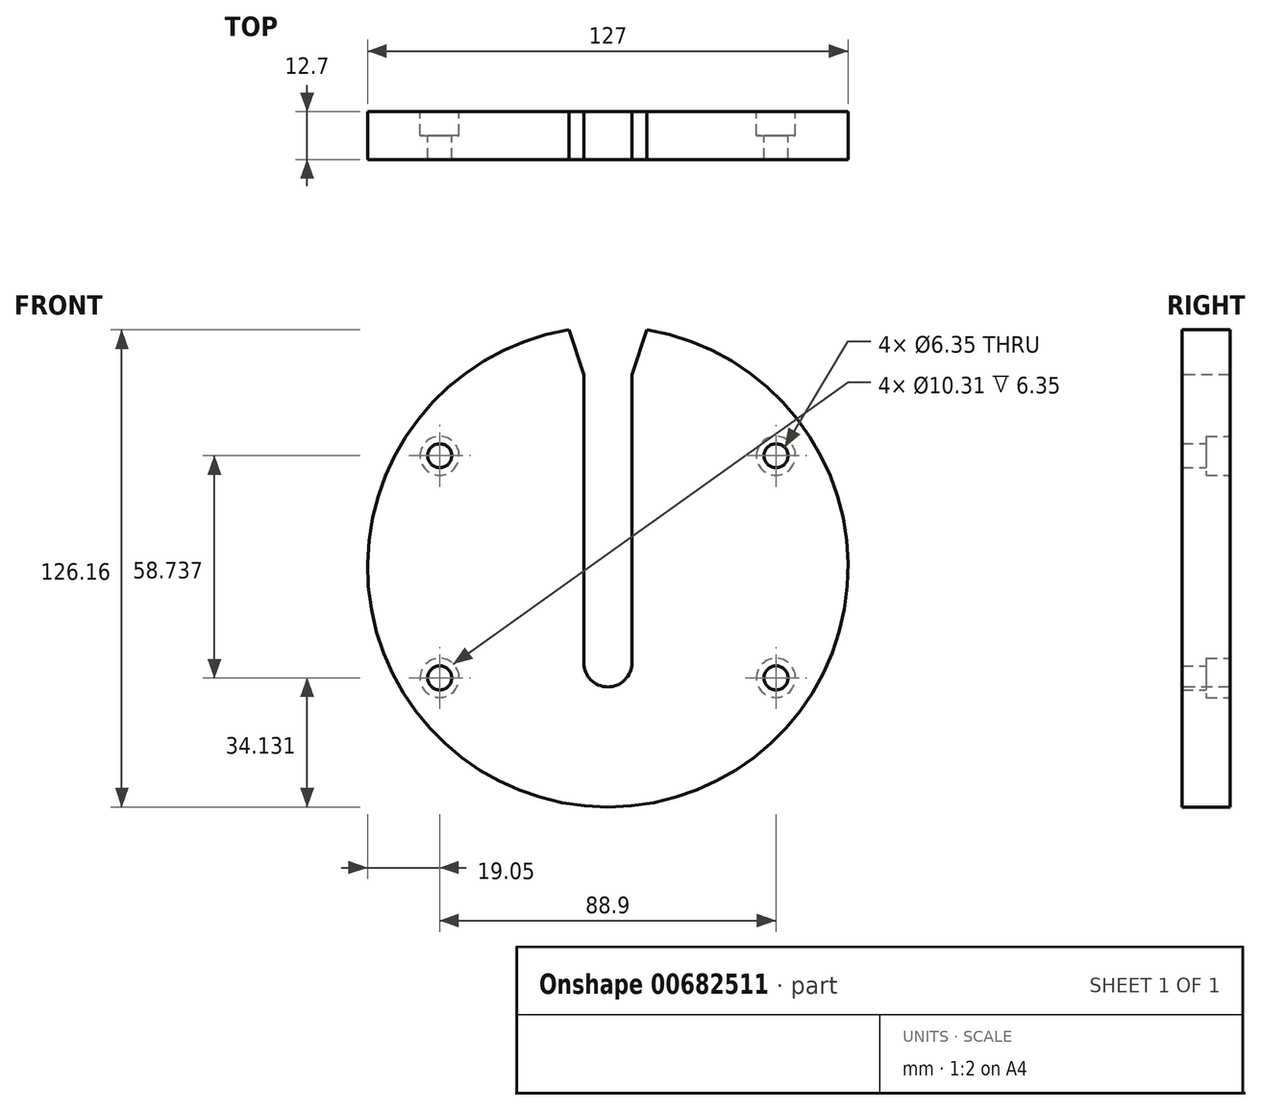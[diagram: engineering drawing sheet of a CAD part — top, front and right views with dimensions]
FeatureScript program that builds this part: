
annotation { "Feature Type Name" : "Feature", "Feature Type Description" : "" }
export const myFeature = defineFeature(function(context is Context, id is Id, definition is map)
    precondition{}
    {
        {
            var Q0;
            Q0=qCreatedBy(makeId("Front.planeOp"),FACE);
            var sketch = newSketch(context, id + "F0", { "sketchPlane" : qUnion([Q0])});
            skPoint(sketch, "E0", {"position": v(-44.45, 29.37) * mm});
            skPoint(sketch, "E1", {"position": v(44.45, 29.37) * mm});
            skPoint(sketch, "E2", {"position": v(44.45, -29.37) * mm});
            skPoint(sketch, "E3", {"position": v(-44.45, -29.37) * mm});
            skLineSegment(sketch, "E4", {"start": v(0, 0) * mm, "end": v(0, 0) * mm});
            skCircle(sketch, "E5", {"center": v(0, 0) * mm, "radius": 63.5 * mm});
            skSolve(sketch);
        }
        {
            var Q0;
            Q0=makeQuery(id+"F0.imprint","IMPRINT",FACE,{"disambiguationData":[TD([[makeQuery(id+"F0.imprint","IMPRINT",EDGE,{"derivedFrom":sQuery(id+"F0.wireOp",EDGE,"0SG29FPq-SwXB-MbIm-qeFK-cjPBrF2aFsSZ.bottom")}),1.0]])]});
            var Q1;
            Q1=makeQuery(id+"F0.imprint","IMPRINT",FACE,{"disambiguationData":[TD([[makeQuery(id+"F0.imprint","IMPRINT",EDGE,{"derivedFrom":sQuery(id+"F0.wireOp",EDGE,"0SG29FPq-SwXB-MbIm-qeFK-cjPBrF2aFsSZ.top")}),-1.0]])]});
            var Q2;
            Q2=makeQuery(id+"F0.imprint","IMPRINT",FACE,{"disambiguationData":[TD([[makeQuery(id+"F0.imprint","IMPRINT",EDGE,{"derivedFrom":sQuery(id+"F0.wireOp",EDGE,"E5")}),1.0]])]});
            extrude(context, id + "F1", {"entities" : qUnion([Q0, Q1, Q2]), "depth" : 12.7 * mm, "offsetDistance" : 25.4 * mm});
        }
        {
            var Q0;
            Q0=makeQuery(id+"F1.opExtrude","CAP_FACE",FACE,{"disambiguationData":[OSD([sQuery(id+"F0.wireOp",EDGE,"E5")])],"isStart":false});
            var sketch = newSketch(context, id + "F2", { "sketchPlane" : qUnion([Q0])});
            skLineSegment(sketch, "E6", {"start": v(-6.35, 50.8) * mm, "end": v(-6.35, -25.4) * mm});
            skLineSegment(sketch, "E7", {"start": v(6.35, -25.4) * mm, "end": v(6.35, 50.8) * mm});
            skArc(sketch, "E8", {"start": v(-6.35, -25.4) * mm, "mid": v(0, -31.75) * mm, "end": v(6.35, -25.4) * mm});
            skLineSegment(sketch, "E9", {"start": v(10.31, 62.66) * mm, "end": v(6.35, 50.8) * mm});
            skLineSegment(sketch, "E10", {"start": v(-6.35, 50.8) * mm, "end": v(-10.31, 62.66) * mm});
            skPoint(sketch, "E11.orphan", {"position": v(6.35, 63.18) * mm});
            skSolve(sketch);
        }
        {
            var Q0;
            {var subQ0=sQuery(id+"F2.wireOp",EDGE,"E6");Q0=makeQuery(id+"F2.imprint","IMPRINT",FACE,{"disambiguationData":[TD([[makeQuery(id+"F2.imprint","IMPRINT",EDGE,{"derivedFrom":subQ0}),1.0]])]});}
            extrude(context, id + "F3", {"entities" : qUnion([Q0]), "operationType" : NewBodyOperationType.REMOVE, "oppositeDirection" : true, "depth" : 25.4 * mm, "offsetDistance" : 25.4 * mm});
        }
        {
            var Q0;
            Q0=sQuery(id+"F0.wireOp",VERTEX,"E1");
            var Q1;
            Q1=sQuery(id+"F0.wireOp",VERTEX,"E0");
            var Q2;
            Q2=sQuery(id+"F0.wireOp",VERTEX,"E2");
            var Q3;
            Q3=sQuery(id+"F0.wireOp",VERTEX,"E3");
            var Q4;
            Q4=makeQuery(id+"F1.opExtrude","SWEPT_BODY",BODY,{"disambiguationData":[OSD([sQuery(id+"F0.wireOp",EDGE,"E5")])]});
            hole(context, id + "F4", {"style" : HoleStyle.C_BORE, "endStyle" : HoleEndStyle.THROUGH, "oppositeDirection" : true, "holeDiameter" : 6.35 * mm, "cBoreDiameter" : 10.3 * mm, "cBoreDepth" : 6.35 * mm, "majorDiameter" : 6.35 * mm, "isTappedThrough" : true, "tappedDepth" : 12.7 * mm, "tapClearance" : 3, "startFromSketch" : true, "locations" : qUnion([Q0, Q1, Q2, Q3]), "scope" : qUnion([Q4])});
        }
    });
